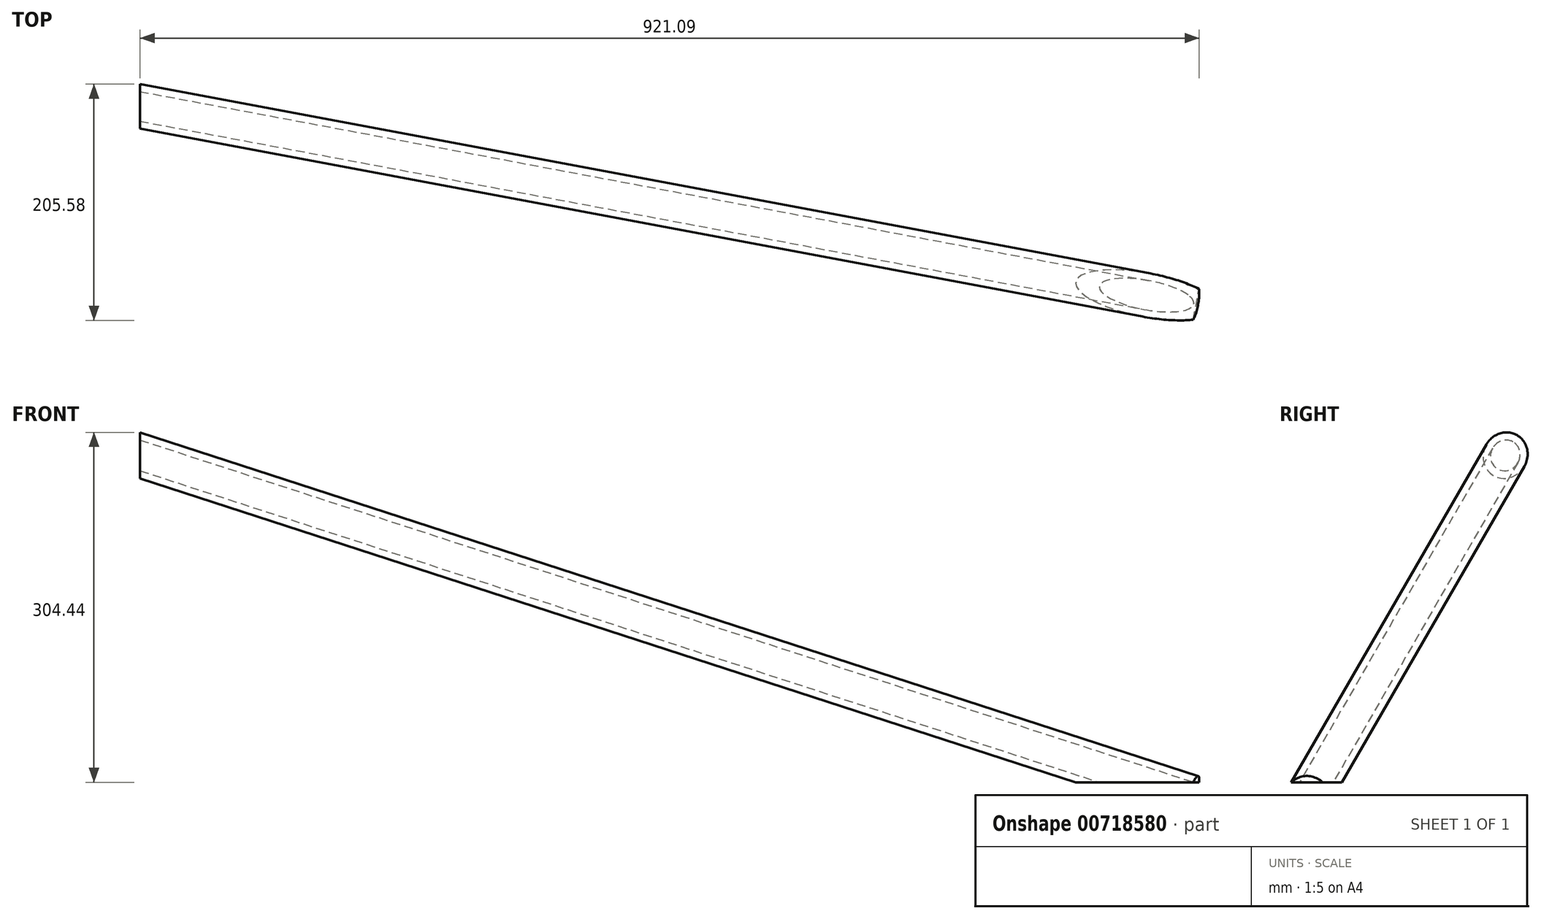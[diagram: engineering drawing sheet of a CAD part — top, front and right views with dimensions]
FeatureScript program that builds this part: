
annotation { "Feature Type Name" : "Feature", "Feature Type Description" : "" }
export const myFeature = defineFeature(function(context is Context, id is Id, definition is map)
    precondition{}
    {
        {
            var Q0;
            Q0=qCreatedBy(makeId("Front.planeOp"),FACE);
            var sketch = newSketch(context, id + "F0", { "sketchPlane" : qUnion([Q0])});
            skLineSegment(sketch, "E0", {"start": v(0, 0) * mm, "end": v(25.61, 78.82) * mm});
            skLineSegment(sketch, "E1", {"start": v(0, 0) * mm, "end": v(-36.28, 62.85) * mm});
            skSolve(sketch);
        }
        {
            var Q0;
            Q0=qCreatedBy(makeId("Right.planeOp"),FACE);
            var sketch = newSketch(context, id + "F1", { "sketchPlane" : qUnion([Q0])});
            skLineSegment(sketch, "E2", {"start": v(0, 0) * mm, "end": v(60.51, 34.94) * mm});
            skLineSegment(sketch, "E3", {"start": v(0, 0) * mm, "end": v(-68.68, 39.65) * mm});
            skSolve(sketch);
        }
        {
            var Q0;
            Q0=sQuery(id+"F1.wireOp",VERTEX,"E2.start");
            var Q1;
            Q1=sQuery(id+"F0.wireOp",VERTEX,"E0.end");
            var Q2;
            Q2=sQuery(id+"F1.wireOp",VERTEX,"E3.end");
            cPlane(context, id + "F2", {"entities" : qUnion([Q0, Q1, Q2]), "cplaneType" : CPlaneType.THREE_POINT, "offset" : 25.4 * mm, "width" : 152.4 * mm, "height" : 152.4 * mm});
        }
        {
            var Q0;
            Q0=qCreatedBy(id+"F2.planeOp",FACE);
            var sketch = newSketch(context, id + "F3", { "sketchPlane" : qUnion([Q0])});
            skCircle(sketch, "E4", {"center": v(0, 0) * mm, "radius": 19.05 * mm});
            skCircle(sketch, "E5", {"center": v(0, 0) * mm, "radius": 12.7 * mm});
            skSolve(sketch);
        }
        {
            var Q0;
            Q0=makeQuery(id+"F3.imprint","IMPRINT",FACE,{"disambiguationData":[TD([[makeQuery(id+"F3.imprint","IMPRINT",EDGE,{"derivedFrom":sQuery(id+"F3.wireOp",EDGE,"E4")}),1.0]])]});
            extrude(context, id + "F4", {"entities" : qUnion([Q0]), "depth" : 990.6 * mm, "offsetDistance" : 25.4 * mm});
        }
        {
            var Q0;
            Q0=qCreatedBy(makeId("Top.planeOp"),FACE);
            cPlane(context, id + "F5", {"entities" : qUnion([Q0]), "cplaneType" : CPlaneType.OFFSET, "offset" : 12.7 * mm, "width" : 152.4 * mm, "height" : 152.4 * mm});
        }
        {
            var Q0;
            Q0=makeQuery(id+"F4.opExtrude","CAP_FACE",FACE,{"disambiguationData":[OSD([sQuery(id+"F3.wireOp",EDGE,"E4")])],"isStart":true});
            var Q1;
            Q1=qCreatedBy(id+"F5.planeOp",FACE);
            extrude(context, id + "F6", {"entities" : qUnion([Q0]), "operationType" : NewBodyOperationType.REMOVE, "endBound" : BoundingType.UP_TO_SURFACE, "oppositeDirection" : true, "depth" : 25.4 * mm, "endBoundEntityFace" : qUnion([Q1]), "offsetDistance" : 25.4 * mm});
        }
        {
            var Q0;
            Q0=qCreatedBy(makeId("Right.planeOp"),FACE);
            cPlane(context, id + "F7", {"entities" : qUnion([Q0]), "cplaneType" : CPlaneType.OFFSET, "offset" : 914.4 * mm, "oppositeDirection" : true, "width" : 152.4 * mm, "height" : 152.4 * mm});
        }
        {
            var Q0;
            Q0=makeQuery(id+"F4.opExtrude","CAP_FACE",FACE,{"disambiguationData":[OSD([sQuery(id+"F3.wireOp",EDGE,"E4"),sQuery(id+"F3.wireOp",EDGE,"E5")])],"isStart":false});
            var Q1;
            Q1=qCreatedBy(id+"F7.planeOp",FACE);
            extrude(context, id + "F8", {"entities" : qUnion([Q0]), "operationType" : NewBodyOperationType.REMOVE, "endBound" : BoundingType.UP_TO_SURFACE, "oppositeDirection" : true, "depth" : 25.4 * mm, "endBoundEntityFace" : qUnion([Q1]), "offsetDistance" : 25.4 * mm});
        }
    });
